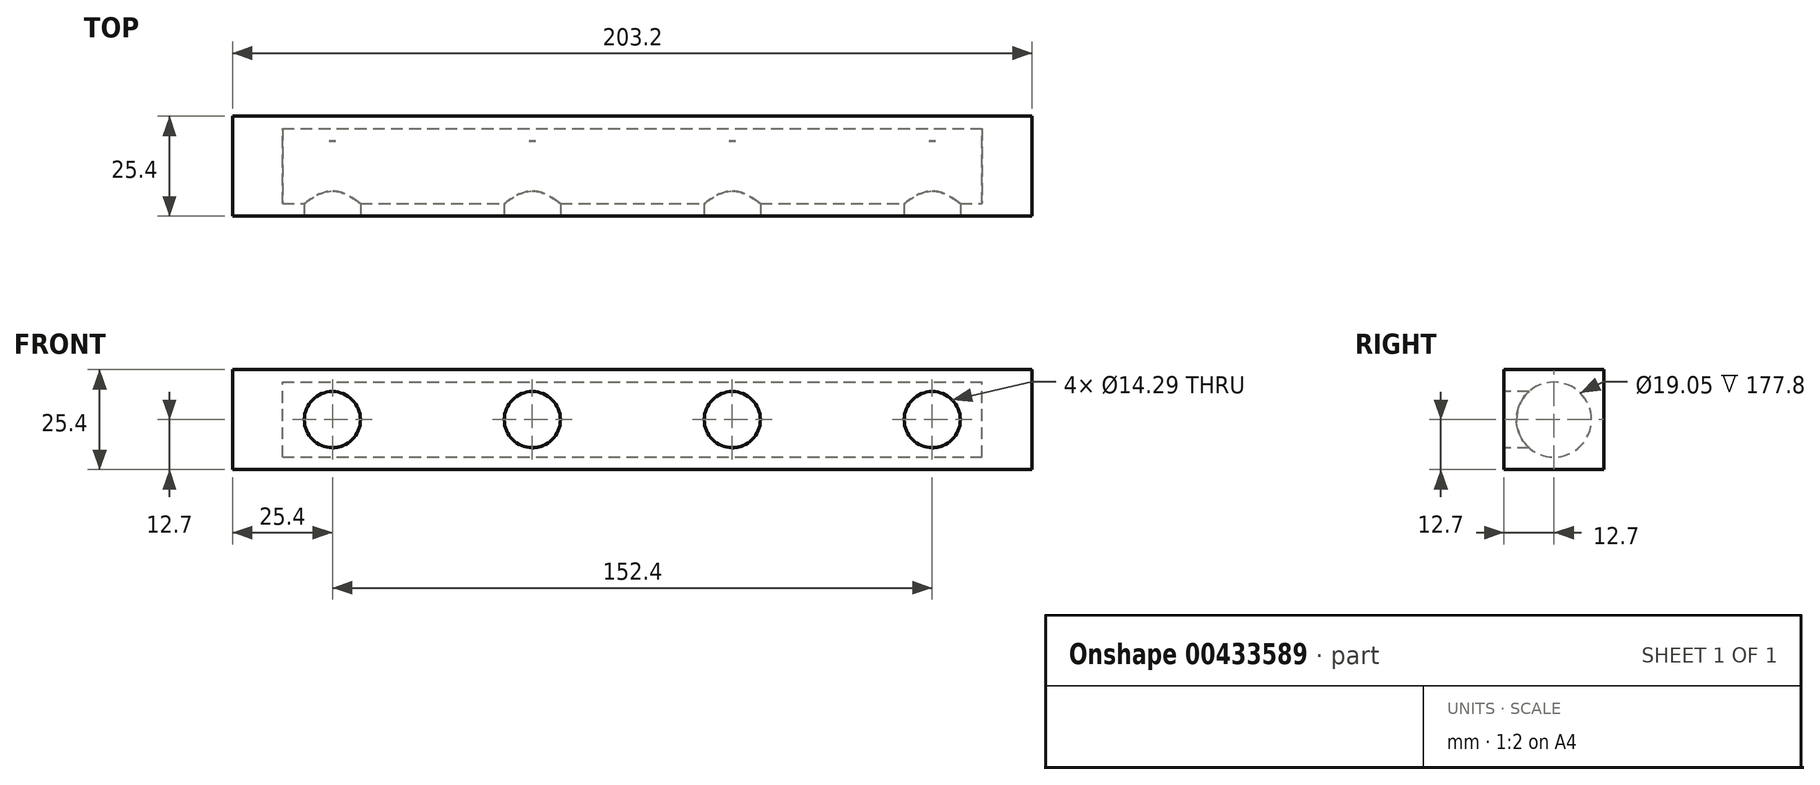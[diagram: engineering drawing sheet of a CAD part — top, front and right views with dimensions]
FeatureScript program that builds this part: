
annotation { "Feature Type Name" : "Feature", "Feature Type Description" : "" }
export const myFeature = defineFeature(function(context is Context, id is Id, definition is map)
    precondition{}
    {
        {
            var Q0;
            Q0=qCreatedBy(makeId("Front.planeOp"),FACE);
            var sketch = newSketch(context, id + "F0", { "sketchPlane" : qUnion([Q0])});
            skLineSegment(sketch, "E0.bottom", {"start": v(-101.6, 12.7) * mm, "end": v(101.6, 12.7) * mm});
            skLineSegment(sketch, "E0.top", {"start": v(-101.6, -12.7) * mm, "end": v(101.6, -12.7) * mm});
            skLineSegment(sketch, "E0.left", {"start": v(-101.6, 12.7) * mm, "end": v(-101.6, -12.7) * mm});
            skLineSegment(sketch, "E0.right", {"start": v(101.6, 12.7) * mm, "end": v(101.6, -12.7) * mm});
            skPoint(sketch, "E0.middle", {"position": v(0, 0) * mm});
            skSolve(sketch);
        }
        {
            var Q0;
            Q0=makeQuery(id+"F0.imprint","IMPRINT",FACE,{"disambiguationData":[TD([[makeQuery(id+"F0.imprint","IMPRINT",EDGE,{"derivedFrom":sQuery(id+"F0.wireOp",EDGE,"E0.bottom")}),-1.0]])]});
            extrude(context, id + "F1", {"entities" : qUnion([Q0]), "depth" : 25.4 * mm});
        }
        {
            var Q0;
            Q0=makeQuery(id+"F1.opExtrude","CAP_FACE",FACE,{"disambiguationData":[OSD([sQuery(id+"F0.wireOp",EDGE,"E0.bottom"),sQuery(id+"F0.wireOp",EDGE,"E0.top"),sQuery(id+"F0.wireOp",EDGE,"E0.left"),sQuery(id+"F0.wireOp",EDGE,"E0.right")])],"isStart":false});
            var sketch = newSketch(context, id + "F2", { "sketchPlane" : qUnion([Q0])});
            skCircle(sketch, "E1", {"center": v(-76.2, 0) * mm, "radius": 7.14 * mm});
            skCircle(sketch, "E2", {"center": v(-25.4, 0) * mm, "radius": 7.14 * mm});
            skCircle(sketch, "E3", {"center": v(25.4, 0) * mm, "radius": 7.14 * mm});
            skCircle(sketch, "E4", {"center": v(76.2, 0) * mm, "radius": 7.14 * mm});
            skSolve(sketch);
        }
        {
            var Q0;
            Q0=makeQuery(id+"F1.opExtrude","SWEPT_FACE",FACE,{"disambiguationData":[OSD([sQuery(id+"F0.wireOp",EDGE,"E0.right")])]});
            var sketch = newSketch(context, id + "F3", { "sketchPlane" : qUnion([Q0])});
            skCircle(sketch, "E5", {"center": v(-12.7, 0) * mm, "radius": 9.53 * mm});
            skPoint(sketch, "E5.centerSnap0", {"position": v(-12.7, 12.7) * mm});
            skSolve(sketch);
        }
        {
            var Q0;
            Q0=makeQuery(id+"F3.imprint","IMPRINT",FACE,{"disambiguationData":[TD([[makeQuery(id+"F3.imprint","IMPRINT",EDGE,{"derivedFrom":sQuery(id+"F3.wireOp",EDGE,"E5")}),1.0]])]});
            extrude(context, id + "F4", {"entities" : qUnion([Q0]), "operationType" : NewBodyOperationType.REMOVE, "oppositeDirection" : true, "depth" : 190.5 * mm});
        }
        {
            var Q0;
            Q0=makeQuery(id+"F1.opExtrude","SWEPT_FACE",FACE,{"disambiguationData":[OSD([sQuery(id+"F0.wireOp",EDGE,"E0.right")])]});
            var sketch = newSketch(context, id + "F5", { "sketchPlane" : qUnion([Q0])});
            skCircle(sketch, "E6", {"center": v(-12.7, 0) * mm, "radius": 9.53 * mm});
            skSolve(sketch);
        }
        {
            var Q0;
            Q0=makeQuery(id+"F5.imprint","IMPRINT",FACE,{"disambiguationData":[TD([[makeQuery(id+"F5.imprint","IMPRINT",EDGE,{"derivedFrom":sQuery(id+"F5.wireOp",EDGE,"E6")}),1.0]])]});
            extrude(context, id + "F6", {"entities" : qUnion([Q0]), "operationType" : NewBodyOperationType.ADD, "oppositeDirection" : true, "depth" : 12.7 * mm});
        }
        {
            var Q0;
            Q0=makeQuery(id+"F2.imprint","IMPRINT",FACE,{"disambiguationData":[TD([[makeQuery(id+"F2.imprint","IMPRINT",EDGE,{"derivedFrom":sQuery(id+"F2.wireOp",EDGE,"E1")}),1.0]])]});
            var Q1;
            Q1=makeQuery(id+"F2.imprint","IMPRINT",FACE,{"disambiguationData":[TD([[makeQuery(id+"F2.imprint","IMPRINT",EDGE,{"derivedFrom":sQuery(id+"F2.wireOp",EDGE,"E2")}),1.0]])]});
            var Q2;
            Q2=makeQuery(id+"F2.imprint","IMPRINT",FACE,{"disambiguationData":[TD([[makeQuery(id+"F2.imprint","IMPRINT",EDGE,{"derivedFrom":sQuery(id+"F2.wireOp",EDGE,"E3")}),1.0]])]});
            var Q3;
            Q3=makeQuery(id+"F2.imprint","IMPRINT",FACE,{"disambiguationData":[TD([[makeQuery(id+"F2.imprint","IMPRINT",EDGE,{"derivedFrom":sQuery(id+"F2.wireOp",EDGE,"E4")}),1.0]])]});
            extrude(context, id + "F7", {"entities" : qUnion([Q0, Q1, Q2, Q3]), "operationType" : NewBodyOperationType.REMOVE, "oppositeDirection" : true, "depth" : 19.05 * mm});
        }
    });
